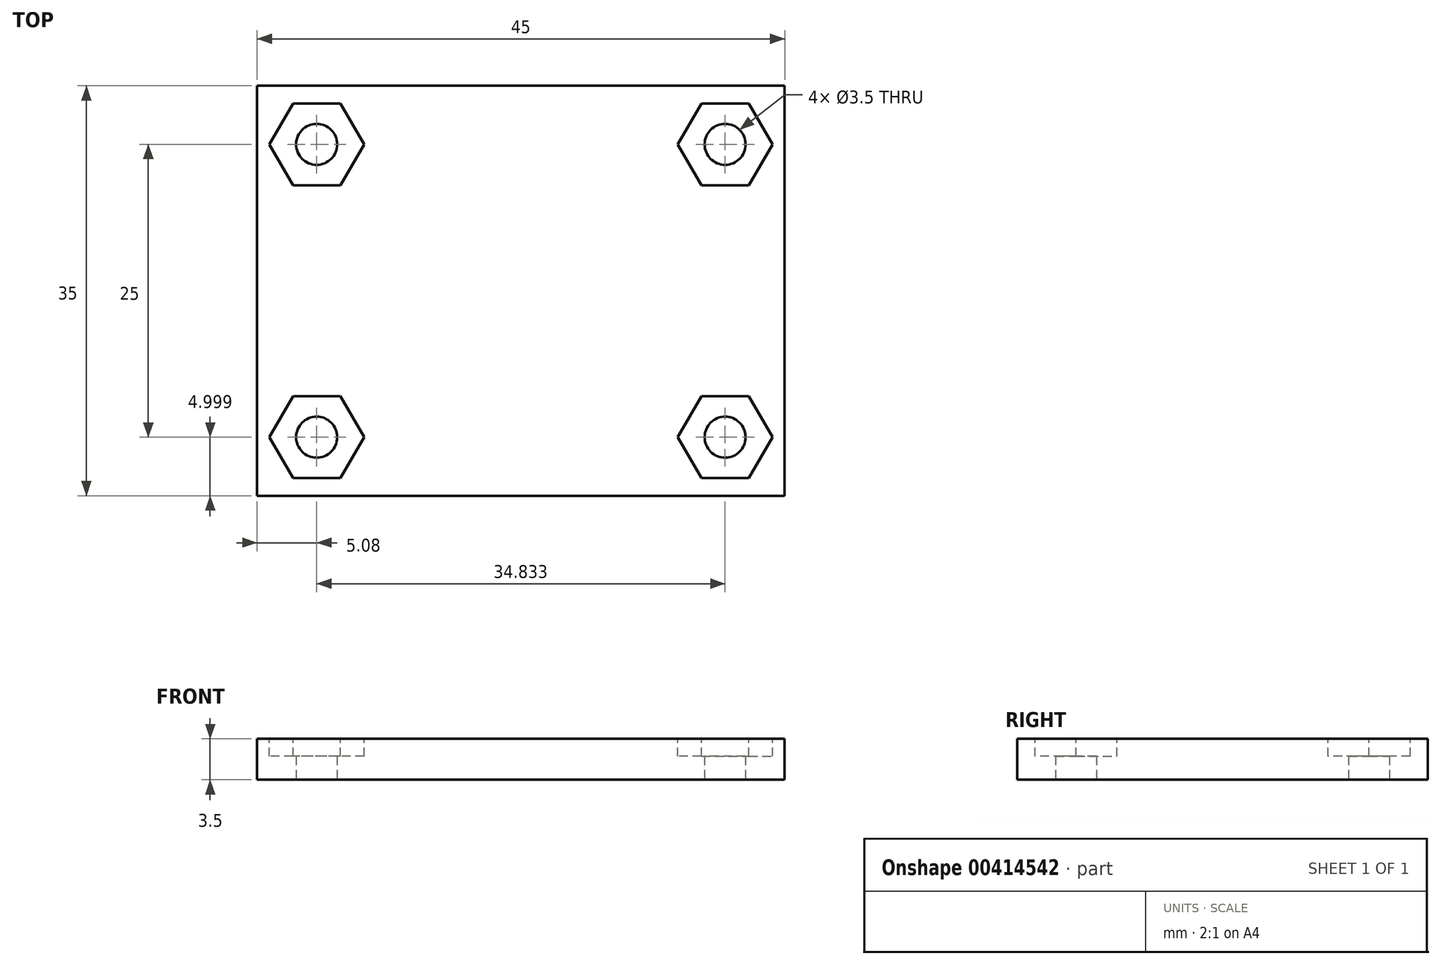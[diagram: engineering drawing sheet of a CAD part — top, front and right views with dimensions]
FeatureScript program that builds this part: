
annotation { "Feature Type Name" : "Feature", "Feature Type Description" : "" }
export const myFeature = defineFeature(function(context is Context, id is Id, definition is map)
    precondition{}
    {
        {
            var Q0;
            Q0=qCreatedBy(makeId("Top.planeOp"),FACE);
            var sketch = newSketch(context, id + "F0", { "sketchPlane" : qUnion([Q0])});
            skLineSegment(sketch, "E0.bottom", {"start": v(-54.78, 5.3) * mm, "end": v(-9.78, 5.3) * mm});
            skLineSegment(sketch, "E0.top", {"start": v(-54.78, -29.7) * mm, "end": v(-9.78, -29.7) * mm});
            skLineSegment(sketch, "E0.left", {"start": v(-54.78, 5.3) * mm, "end": v(-54.78, -29.7) * mm});
            skLineSegment(sketch, "E0.right", {"start": v(-9.78, 5.3) * mm, "end": v(-9.78, -29.7) * mm});
            skLineSegment(sketch, "E1", {"start": v(-32.28, 5.3) * mm, "end": v(-32.28, -29.7) * mm, "construction": true});
            skLineSegment(sketch, "E2", {"start": v(-54.78, -12.2) * mm, "end": v(-9.78, -12.2) * mm, "construction": true});
            skSolve(sketch);
        }
        {
            var Q0;
            Q0=makeQuery(id+"F0.imprint","IMPRINT",FACE,{"disambiguationData":[TD([[makeQuery(id+"F0.imprint","IMPRINT",EDGE,{"derivedFrom":sQuery(id+"F0.wireOp",EDGE,"E0.bottom")}),-1.0]])]});
            var sketch = newSketch(context, id + "F1", { "sketchPlane" : qUnion([Q0])});
            skLineSegment(sketch, "E3", {"start": v(-54.24, 0.3) * mm, "end": v(-49.7, 0.3) * mm, "construction": true});
            skLineSegment(sketch, "E4", {"start": v(-49.78, 40.23) * mm, "end": v(-49.7, 0.3) * mm, "construction": true});
            skCircle(sketch, "E5", {"center": v(-49.7, 0.3) * mm, "radius": 1.75 * mm});
            skCircle(sketch, "E6.MirrorC", {"center": v(-14.87, 0.3) * mm, "radius": 1.75 * mm});
            skCircle(sketch, "E7.MirrorC", {"center": v(-14.87, -24.7) * mm, "radius": 1.75 * mm});
            skCircle(sketch, "E8.MirrorC", {"center": v(-49.7, -24.7) * mm, "radius": 1.75 * mm});
            skSolve(sketch);
        }
        {
            var Q0;
            Q0=makeQuery(id+"F1.imprint","IMPRINT",FACE,{"disambiguationData":[TD([[makeQuery(id+"F1.imprint","IMPRINT",EDGE,{"derivedFrom":sQuery(id+"F1.wireOp",EDGE,"E5")}),-1.0]])]});
            extrude(context, id + "F2", {"entities" : qUnion([Q0]), "depth" : 3.5 * mm});
        }
        {
            var Q0;
            Q0=makeQuery(id+"F2.opExtrude","CAP_FACE",FACE,{"disambiguationData":[OSD([sQuery(id+"F0.wireOp",EDGE,"E0.bottom"),sQuery(id+"F0.wireOp",EDGE,"E0.top"),sQuery(id+"F0.wireOp",EDGE,"E0.left"),sQuery(id+"F0.wireOp",EDGE,"E0.right"),sQuery(id+"F1.wireOp",EDGE,"E5"),sQuery(id+"F1.wireOp",EDGE,"E6.MirrorC"),sQuery(id+"F1.wireOp",EDGE,"E7.MirrorC"),sQuery(id+"F1.wireOp",EDGE,"E8.MirrorC")])],"isStart":false});
            var sketch = newSketch(context, id + "F3", { "sketchPlane" : qUnion([Q0])});
            skLineSegment(sketch, "E9", {"start": v(-9.78, -12.2) * mm, "end": v(-54.78, -12.2) * mm, "construction": true});
            skLineSegment(sketch, "E10", {"start": v(-32.28, 5.3) * mm, "end": v(-32.28, -29.7) * mm, "construction": true});
            skCircle(sketch, "E11.MirrorC", {"center": v(-14.87, 0.3) * mm, "radius": 3.5 * mm, "construction": true});
            skLineSegment(sketch, "E12.MirrorCS", {"start": v(-18.9, 0.3) * mm, "end": v(-16.89, -3.2) * mm});
            skLineSegment(sketch, "E13.MirrorCS", {"start": v(-16.89, -3.2) * mm, "end": v(-12.85, -3.2) * mm});
            skPoint(sketch, "E14.MirrorP", {"position": v(-14.87, -3.2) * mm});
            skLineSegment(sketch, "E15.MirrorCS", {"start": v(-12.85, -3.2) * mm, "end": v(-10.83, 0.3) * mm});
            skLineSegment(sketch, "E16.MirrorCS", {"start": v(-10.83, 0.3) * mm, "end": v(-12.85, 3.8) * mm});
            skLineSegment(sketch, "E17.MirrorCS", {"start": v(-12.85, 3.8) * mm, "end": v(-16.89, 3.8) * mm});
            skLineSegment(sketch, "E18.MirrorCS", {"start": v(-16.89, 3.8) * mm, "end": v(-18.9, 0.3) * mm});
            skPoint(sketch, "E19.MirrorP", {"position": v(-49.7, -21.2) * mm});
            skLineSegment(sketch, "E20.MirrorCS", {"start": v(-47.68, -21.2) * mm, "end": v(-51.72, -21.2) * mm});
            skCircle(sketch, "E21.MirrorC", {"center": v(-49.7, -24.7) * mm, "radius": 3.5 * mm, "construction": true});
            skLineSegment(sketch, "E22.MirrorCS", {"start": v(-45.66, -24.7) * mm, "end": v(-47.68, -21.2) * mm});
            skLineSegment(sketch, "E23.MirrorCS", {"start": v(-47.68, -28.2) * mm, "end": v(-45.66, -24.7) * mm});
            skLineSegment(sketch, "E24.MirrorCS", {"start": v(-51.72, -28.2) * mm, "end": v(-47.68, -28.2) * mm});
            skLineSegment(sketch, "E25.MirrorCS", {"start": v(-51.72, -21.2) * mm, "end": v(-53.74, -24.7) * mm});
            skLineSegment(sketch, "E26.MirrorCS", {"start": v(-53.74, -24.7) * mm, "end": v(-51.72, -28.2) * mm});
            skPoint(sketch, "E27.MirrorP", {"position": v(-14.87, -21.2) * mm});
            skLineSegment(sketch, "E28.MirrorCS", {"start": v(-16.89, -21.2) * mm, "end": v(-12.85, -21.2) * mm});
            skLineSegment(sketch, "E29.MirrorCS", {"start": v(-12.85, -21.2) * mm, "end": v(-10.83, -24.7) * mm});
            skLineSegment(sketch, "E30.MirrorCS", {"start": v(-10.83, -24.7) * mm, "end": v(-12.85, -28.2) * mm});
            skLineSegment(sketch, "E31.MirrorCS", {"start": v(-12.85, -28.2) * mm, "end": v(-16.89, -28.2) * mm});
            skLineSegment(sketch, "E32.MirrorCS", {"start": v(-18.9, -24.7) * mm, "end": v(-16.89, -21.2) * mm});
            skLineSegment(sketch, "E33.MirrorCS", {"start": v(-16.89, -28.2) * mm, "end": v(-18.9, -24.7) * mm});
            skCircle(sketch, "E34.MirrorC", {"center": v(-14.87, -24.7) * mm, "radius": 3.5 * mm, "construction": true});
            skLineSegment(sketch, "E35.MirrorCS", {"start": v(-47.68, 3.8) * mm, "end": v(-45.66, 0.3) * mm});
            skCircle(sketch, "E36.MirrorC", {"center": v(-49.7, 0.3) * mm, "radius": 3.5 * mm, "construction": true});
            skLineSegment(sketch, "E37.MirrorCS", {"start": v(-51.72, -3.2) * mm, "end": v(-53.74, 0.3) * mm});
            skLineSegment(sketch, "E38.MirrorCS", {"start": v(-47.68, -3.2) * mm, "end": v(-51.72, -3.2) * mm});
            skLineSegment(sketch, "E39.MirrorCS", {"start": v(-45.66, 0.3) * mm, "end": v(-47.68, -3.2) * mm});
            skLineSegment(sketch, "E40.MirrorCS", {"start": v(-51.72, 3.8) * mm, "end": v(-47.68, 3.8) * mm});
            skPoint(sketch, "E41.MirrorP", {"position": v(-49.7, -3.2) * mm});
            skLineSegment(sketch, "E42.MirrorCS", {"start": v(-53.74, 0.3) * mm, "end": v(-51.72, 3.8) * mm});
            skSolve(sketch);
        }
        {
            var Q0;
            Q0=makeQuery(id+"F3.imprint","IMPRINT",FACE,{"disambiguationData":[TD([[makeQuery(id+"F3.imprint","IMPRINT",EDGE,{"derivedFrom":sQuery(id+"F3.wireOp",EDGE,"E20.MirrorCS")}),1.0]])]});
            var Q1;
            Q1=makeQuery(id+"F3.imprint","IMPRINT",FACE,{"disambiguationData":[TD([[makeQuery(id+"F3.imprint","IMPRINT",EDGE,{"derivedFrom":sQuery(id+"F3.wireOp",EDGE,"E35.MirrorCS")}),-1.0]])]});
            var Q2;
            Q2=makeQuery(id+"F3.imprint","IMPRINT",FACE,{"disambiguationData":[TD([[makeQuery(id+"F3.imprint","IMPRINT",EDGE,{"derivedFrom":sQuery(id+"F3.wireOp",EDGE,"E12.MirrorCS")}),1.0]])]});
            var Q3;
            Q3=makeQuery(id+"F3.imprint","IMPRINT",FACE,{"disambiguationData":[TD([[makeQuery(id+"F3.imprint","IMPRINT",EDGE,{"derivedFrom":sQuery(id+"F3.wireOp",EDGE,"E28.MirrorCS")}),-1.0]])]});
            extrude(context, id + "F4", {"entities" : qUnion([Q0, Q1, Q2, Q3]), "operationType" : NewBodyOperationType.REMOVE, "oppositeDirection" : true, "depth" : 1.5 * mm});
        }
    });
